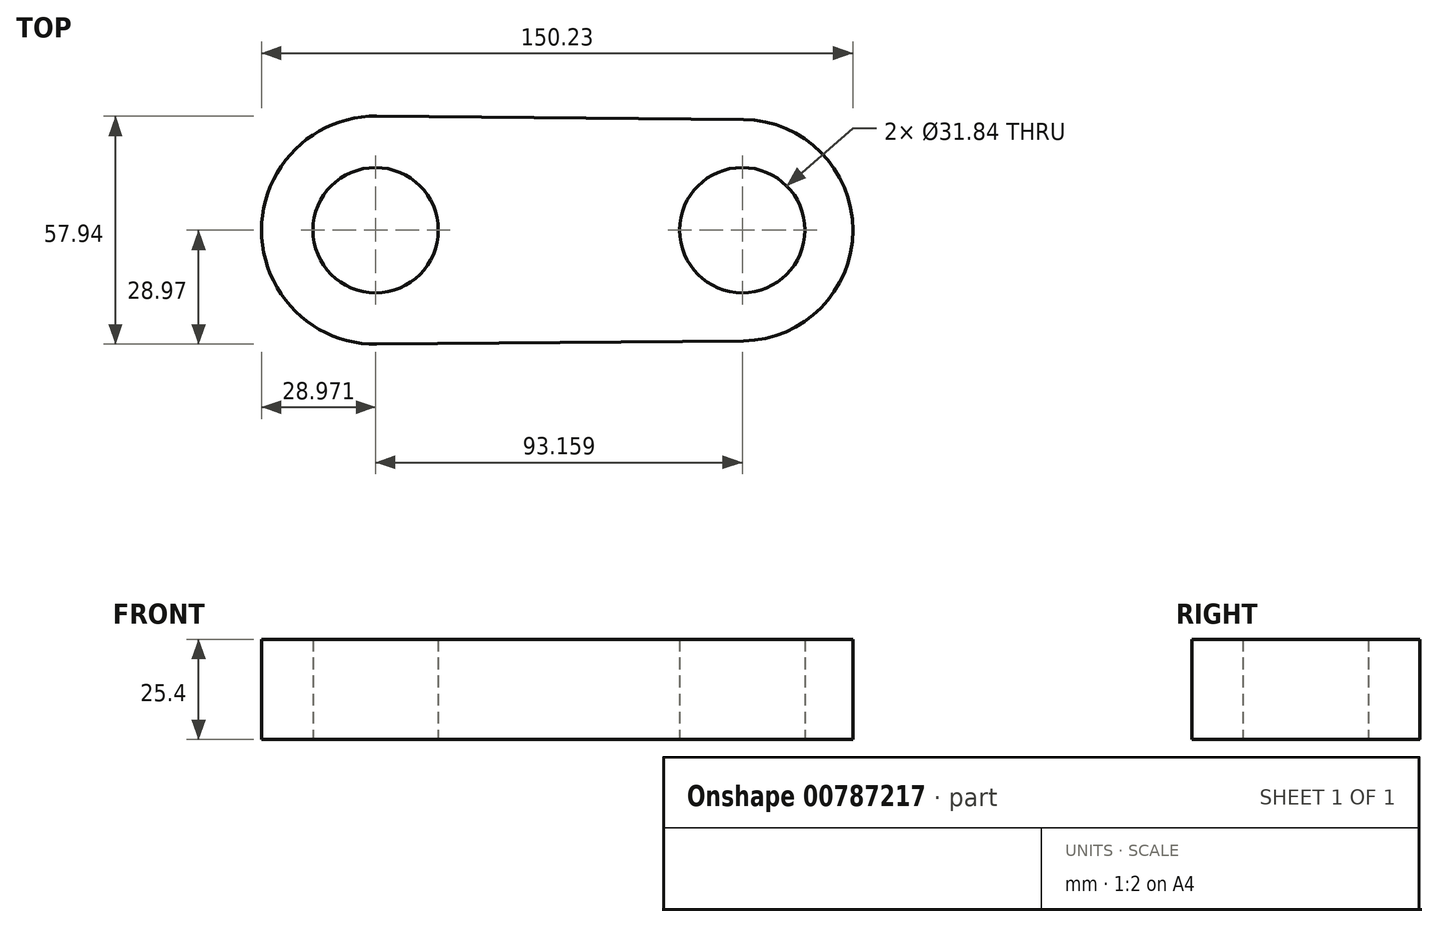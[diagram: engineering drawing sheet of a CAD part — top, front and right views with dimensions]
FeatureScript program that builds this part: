
annotation { "Feature Type Name" : "Feature", "Feature Type Description" : "" }
export const myFeature = defineFeature(function(context is Context, id is Id, definition is map)
    precondition{}
    {
        {
            var Q0;
            Q0=qCreatedBy(makeId("Top.planeOp"),FACE);
            var sketch = newSketch(context, id + "F0", { "sketchPlane" : qUnion([Q0])});
            skCircle(sketch, "E0", {"center": v(-46.58, 0) * mm, "radius": 15.92 * mm});
            skCircle(sketch, "E1", {"center": v(46.58, 0) * mm, "radius": 15.92 * mm});
            skArc(sketch, "E2", {"start": v(-46.3, 28.97) * mm, "mid": v(-75.55, 0) * mm, "end": v(-46.3, -28.97) * mm});
            skArc(sketch, "E3", {"start": v(46.84, -28.1) * mm, "mid": v(74.68, 0) * mm, "end": v(46.84, 28.1) * mm});
            skLineSegment(sketch, "E4", {"start": v(-46.3, 28.97) * mm, "end": v(46.84, 28.1) * mm});
            skLineSegment(sketch, "E5", {"start": v(46.84, -28.1) * mm, "end": v(-46.3, -28.97) * mm});
            skArc(sketch, "E6", {"start": v(-46.3, -28.97) * mm, "mid": v(-17.6, 0) * mm, "end": v(-46.3, 28.97) * mm});
            skSolve(sketch);
        }
        {
            var Q0;
            Q0=makeQuery(id+"F0.imprint","IMPRINT",FACE,{"disambiguationData":[TD([[makeQuery(id+"F0.imprint","IMPRINT",EDGE,{"derivedFrom":sQuery(id+"F0.wireOp",EDGE,"E0")}),-1.0]])]});
            var Q1;
            Q1=makeQuery(id+"F0.imprint","IMPRINT",FACE,{"disambiguationData":[TD([[makeQuery(id+"F0.imprint","IMPRINT",EDGE,{"derivedFrom":sQuery(id+"F0.wireOp",EDGE,"E1")}),-1.0]])]});
            extrude(context, id + "F1", {"entities" : qUnion([Q0, Q1]), "depth" : 25.4 * mm, "offsetDistance" : 25.4 * mm});
        }
        {
            var Q0;
            Q0=sQuery(id+"F0.wireOp",EDGE,"E6");
            var Q1;
            Q1=sQuery(id+"F0.wireOp",EDGE,"E2");
            var Q2;
            Q2=sQuery(id+"F0.wireOp",EDGE,"E0");
            extrude(context, id + "F2", {"bodyType" : ToolBodyType.SURFACE, "surfaceEntities" : qUnion([Q0, Q1, Q2]), "depth" : 50.8 * mm, "offsetDistance" : 25.4 * mm});
        }
    });
